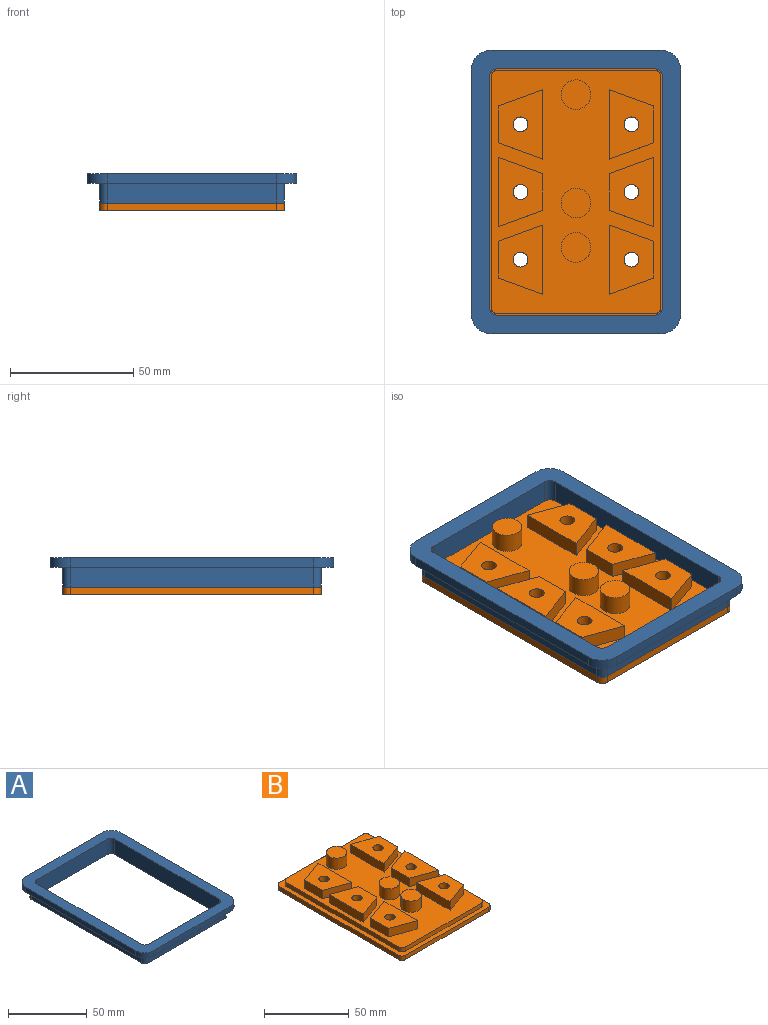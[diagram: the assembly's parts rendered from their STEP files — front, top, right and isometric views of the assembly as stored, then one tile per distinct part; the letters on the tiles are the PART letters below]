
ASSEMBLY  parts=2 mates=1
PART A: 27 faces, bbox 85x115x12 mm
  f0: plane 69x4mm, normal (0,1,0), area 276mm2, adj f8,f9,f10,f13
  f1: plane 99x4mm, normal (-1,0,0), area 396mm2, adj f8,f9,f10,f11
  f2: plane 69x4mm, normal (0,-1,0), area 276mm2, adj f8,f9,f11,f12
  f3: plane 94x12mm, normal (1,0,0), area 1128mm2, adj f8,f14,f17,f26
  f4: plane 64x12mm, normal (0,-1,0), area 768mm2, adj f8,f14,f15,f26
  f5: plane 94x12mm, normal (-1,0,0), area 1128mm2, adj f8,f15,f16,f26
  f6: plane 64x12mm, normal (0,1,0), area 768mm2, adj f8,f16,f17,f26
  f7: plane 99x4mm, normal (1,0,0), area 396mm2, adj f8,f9,f12,f13
  f8: plane 115x85mm, normal (0,0,1), area 2727.8mm2, adj f0,f1,f2,f3,f4,f5,f6,f7
  f9: plane 115x85mm, normal (0,0,-1), area 1852.8mm2, adj f0,f1,f2,f7,f10,f11,f12,f13
  f10: cylinder r=8mm len=8mm, axis (0,0,1), area 50.3mm2, adj f0,f1,f8,f9
  f11: cylinder r=8mm len=8mm, axis (0,0,-1), area 50.3mm2, adj f1,f2,f8,f9
  f12: cylinder r=8mm len=8mm, axis (0,0,1), area 50.3mm2, adj f2,f7,f8,f9
  f13: cylinder r=8mm len=8mm, axis (0,0,-1), area 50.3mm2, adj f0,f7,f8,f9
  f14: cylinder r=3mm len=12mm, axis (0,0,-1), area 56.5mm2, adj f3,f4,f8,f26
  f15: cylinder r=3mm len=12mm, axis (0,0,1), area 56.5mm2, adj f4,f5,f8,f26
  f16: cylinder r=3mm len=12mm, axis (0,0,-1), area 56.5mm2, adj f5,f6,f8,f26
  f17: cylinder r=3mm len=12mm, axis (0,0,1), area 56.5mm2, adj f3,f6,f8,f26
  f18: plane 99x8mm, normal (-1,0,0), area 792mm2, adj f9,f19,f25,f26
  f19: cylinder r=3mm len=8mm, axis (0,0,1), area 37.7mm2, adj f9,f18,f20,f26
  f20: plane 69x8mm, normal (0,1,0), area 552mm2, adj f9,f19,f21,f26
  f21: cylinder r=3mm len=8mm, axis (0,0,1), area 37.7mm2, adj f9,f20,f22,f26
  f22: plane 99x8mm, normal (1,0,0), area 792mm2, adj f9,f21,f23,f26
  f23: cylinder r=3mm len=8mm, axis (0,0,1), area 37.7mm2, adj f9,f22,f24,f26
  f24: plane 69x8mm, normal (0,-1,0), area 552mm2, adj f9,f23,f25,f26
  f25: cylinder r=3mm len=8mm, axis (0,0,1), area 37.7mm2, adj f9,f18,f24,f26
  f26: plane 105x75mm, normal (0,0,-1), area 875mm2, adj f3,f4,f5,f6,f14,f15,f16,f17
PART B: 61 faces, bbox 75x105x14 mm
  f0: plane 105x75mm, normal (0,0,-1), area 7697.6mm2, adj f3,f4,f7,f11,f12,f17,f22,f29
  f1: plane 99x69mm, normal (0,0,1), area 4156.4mm2, adj f5,f6,f8,f9,f10,f13,f14,f15
  f2: plane 105x75mm, normal (0,0,1), area 1044mm2, adj f3,f4,f5,f6,f7,f8,f9,f10
  f3: plane 69x3mm, normal (0,1,0), area 207mm2, adj f0,f2,f11,f35
  f4: plane 69x3mm, normal (0,-1,0), area 207mm2, adj f0,f2,f12,f36
  f5: plane 63x3mm, normal (0,1,0), area 189mm2, adj f1,f2,f9,f33
  f6: plane 63x3mm, normal (0,-1,0), area 189mm2, adj f1,f2,f10,f34
  f7: plane 99x3mm, normal (-1,0,0), area 297mm2, adj f0,f2,f11,f12
  f8: plane 93x3mm, normal (-1,0,0), area 279mm2, adj f1,f2,f9,f10
  f9: cylinder r=3mm len=3mm, axis (0,0,1), area 14.1mm2, adj f1,f2,f5,f8
  f10: cylinder r=3mm len=3mm, axis (0,0,-1), area 14.1mm2, adj f1,f2,f6,f8
  f11: cylinder r=3mm len=3mm, axis (0,0,1), area 14.1mm2, adj f0,f2,f3,f7
  f12: cylinder r=3mm len=3mm, axis (0,0,-1), area 14.1mm2, adj f0,f2,f4,f7
  f13: plane 28.1x6mm, normal (1,0,0), area 168.6mm2, adj f1,f14,f16,f18
  f14: plane 18x6.55mm, normal (-0.34,0.94,0), area 114.9mm2, adj f1,f13,f15,f18
  f15: plane 15x6mm, normal (-1,0,0), area 90mm2, adj f1,f14,f16,f18
  f16: plane 18x6.55mm, normal (-0.34,-0.94,0), area 114.9mm2, adj f1,f13,f15,f18
  f17: cylinder r=3mm len=12mm, axis (0,0,-1), area 226.2mm2, adj f0,f18
  f18: plane 28.1x18mm, normal (0,0,1), area 359.7mm2, adj f13,f14,f15,f16,f17
  f19: plane 28.1x6mm, normal (1,0,0), area 168.6mm2, adj f1,f20,f23,f24
  f20: plane 18x6.55mm, normal (-0.34,0.94,0), area 114.9mm2, adj f1,f19,f21,f24
  f21: plane 15x6mm, normal (-1,0,0), area 90mm2, adj f1,f20,f23,f24
  f22: cylinder r=3mm len=12mm, axis (0,0,-1), area 226.2mm2, adj f0,f24
  f23: plane 18x6.55mm, normal (-0.34,-0.94,0), area 114.9mm2, adj f1,f19,f21,f24
  f24: plane 28.1x18mm, normal (0,0,1), area 359.7mm2, adj f19,f20,f21,f22,f23
  f25: plane 15x6mm, normal (1,0,0), area 90mm2, adj f1,f26,f28,f30
  f26: plane 18x6.55mm, normal (0.34,0.94,0), area 114.9mm2, adj f1,f25,f27,f30
  f27: plane 28.1x6mm, normal (-1,0,0), area 168.6mm2, adj f1,f26,f28,f30
  f28: plane 18x6.55mm, normal (0.34,-0.94,0), area 114.9mm2, adj f1,f25,f27,f30
  f29: cylinder r=3mm len=12mm, axis (0,0,-1), area 226.2mm2, adj f0,f30
  f30: plane 28.1x18mm, normal (0,0,1), area 359.7mm2, adj f25,f26,f27,f28,f29
  f31: plane 99x3mm, normal (1,0,0), area 297mm2, adj f0,f2,f35,f36
  f32: plane 93x3mm, normal (1,0,0), area 279mm2, adj f1,f2,f33,f34
  f33: cylinder r=3mm len=3mm, axis (0,0,1), area 14.1mm2, adj f1,f2,f5,f32
  f34: cylinder r=3mm len=3mm, axis (0,0,-1), area 14.1mm2, adj f1,f2,f6,f32
  f35: cylinder r=3mm len=3mm, axis (0,0,1), area 14.1mm2, adj f0,f2,f3,f31
  f36: cylinder r=3mm len=3mm, axis (0,0,-1), area 14.1mm2, adj f0,f2,f4,f31
  f37: plane 28.1x6mm, normal (-1,0,0), area 168.6mm2, adj f1,f38,f40,f42
  f38: plane 18x6.55mm, normal (0.34,0.94,0), area 114.9mm2, adj f1,f37,f39,f42
  f39: plane 15x6mm, normal (1,0,0), area 90mm2, adj f1,f38,f40,f42
  f40: plane 18x6.55mm, normal (0.34,-0.94,0), area 114.9mm2, adj f1,f37,f39,f42
  f41: cylinder r=3mm len=12mm, axis (0,0,-1), area 226.2mm2, adj f0,f42
  f42: plane 28.1x18mm, normal (0,0,1), area 359.7mm2, adj f37,f38,f39,f40,f41
  f43: plane 28.1x6mm, normal (-1,0,0), area 168.6mm2, adj f1,f44,f47,f48
  f44: plane 18x6.55mm, normal (0.34,0.94,0), area 114.9mm2, adj f1,f43,f45,f48
  f45: plane 15x6mm, normal (1,0,0), area 90mm2, adj f1,f44,f47,f48
  f46: cylinder r=3mm len=12mm, axis (0,0,-1), area 226.2mm2, adj f0,f48
  f47: plane 18x6.55mm, normal (0.34,-0.94,0), area 114.9mm2, adj f1,f43,f45,f48
  f48: plane 28.1x18mm, normal (0,0,1), area 359.7mm2, adj f43,f44,f45,f46,f47
  f49: plane 15x6mm, normal (-1,0,0), area 90mm2, adj f1,f50,f52,f54
  f50: plane 18x6.55mm, normal (-0.34,0.94,0), area 114.9mm2, adj f1,f49,f51,f54
  f51: plane 28.1x6mm, normal (1,0,0), area 168.6mm2, adj f1,f50,f52,f54
  f52: plane 18x6.55mm, normal (-0.34,-0.94,0), area 114.9mm2, adj f1,f49,f51,f54
  f53: cylinder r=3mm len=12mm, axis (0,0,-1), area 226.2mm2, adj f0,f54
  f54: plane 28.1x18mm, normal (0,0,1), area 359.7mm2, adj f49,f50,f51,f52,f53
  f55: cylinder r=6mm len=12mm, axis (0,0,-1), area 301.6mm2, adj f1,f56
  f56: plane 12x12mm, normal (0,0,1), area 113.1mm2, adj f55
  f57: cylinder r=6mm len=12mm, axis (0,0,-1), area 301.6mm2, adj f1,f58
  f58: plane 12x12mm, normal (0,0,1), area 113.1mm2, adj f57
  f59: cylinder r=6mm len=12mm, axis (0,0,-1), area 301.6mm2, adj f1,f60
  f60: plane 12x12mm, normal (0,0,1), area 113.1mm2, adj f59
PLACE A at identity
PLACE B t=(0,0,-11)mm
MATE fastened B.f2 <-> A.f26  axis (0,0,1) through (-34.5,-52.5,-8)mm
